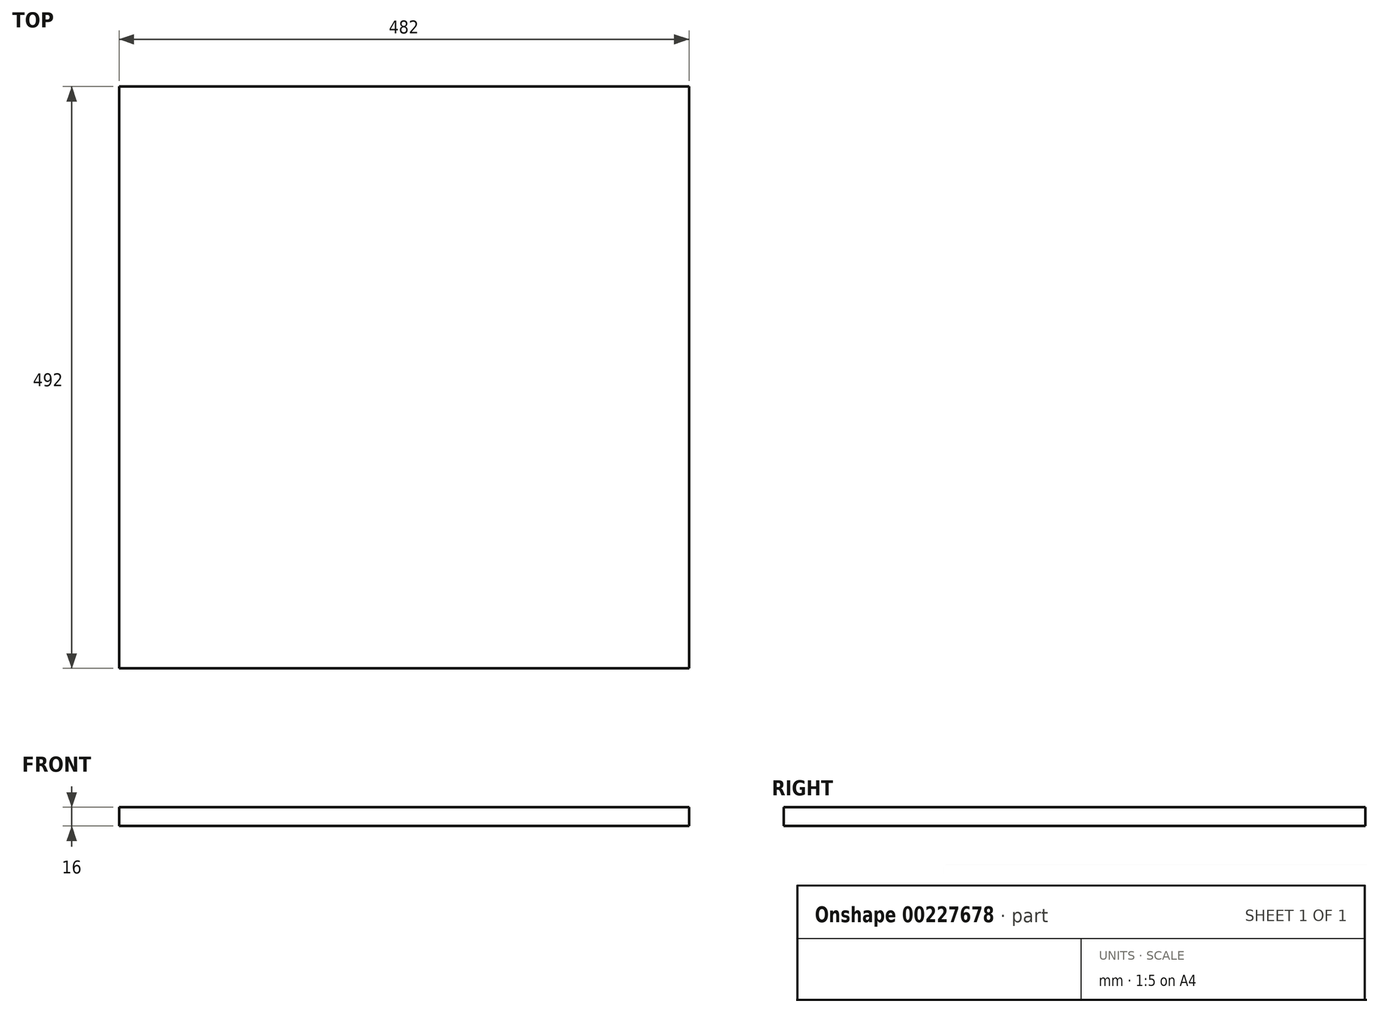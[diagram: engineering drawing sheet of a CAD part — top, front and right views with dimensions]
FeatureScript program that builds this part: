
annotation { "Feature Type Name" : "Feature", "Feature Type Description" : "" }
export const myFeature = defineFeature(function(context is Context, id is Id, definition is map)
    precondition{}
    {
        {
            var Q0;
            Q0=qCreatedBy(makeId("Top.planeOp"),FACE);
            var sketch = newSketch(context, id + "F0", { "sketchPlane" : qUnion([Q0])});
            skLineSegment(sketch, "E0.bottom", {"start": v(241, -246) * mm, "end": v(-241, -246) * mm});
            skLineSegment(sketch, "E0.top", {"start": v(241, 246) * mm, "end": v(-241, 246) * mm});
            skLineSegment(sketch, "E0.left", {"start": v(241, -246) * mm, "end": v(241, 246) * mm});
            skLineSegment(sketch, "E0.right", {"start": v(-241, -246) * mm, "end": v(-241, 246) * mm});
            skPoint(sketch, "E0.middle", {"position": v(0, 0) * mm});
            skSolve(sketch);
        }
        {
            var Q0;
            Q0 = qSketchRegion(id + "F0", true);
            extrude(context, id + "F1", {"entities" : qUnion([Q0]), "depth" : 16 * mm, "symmetric" : true});
        }
    });
